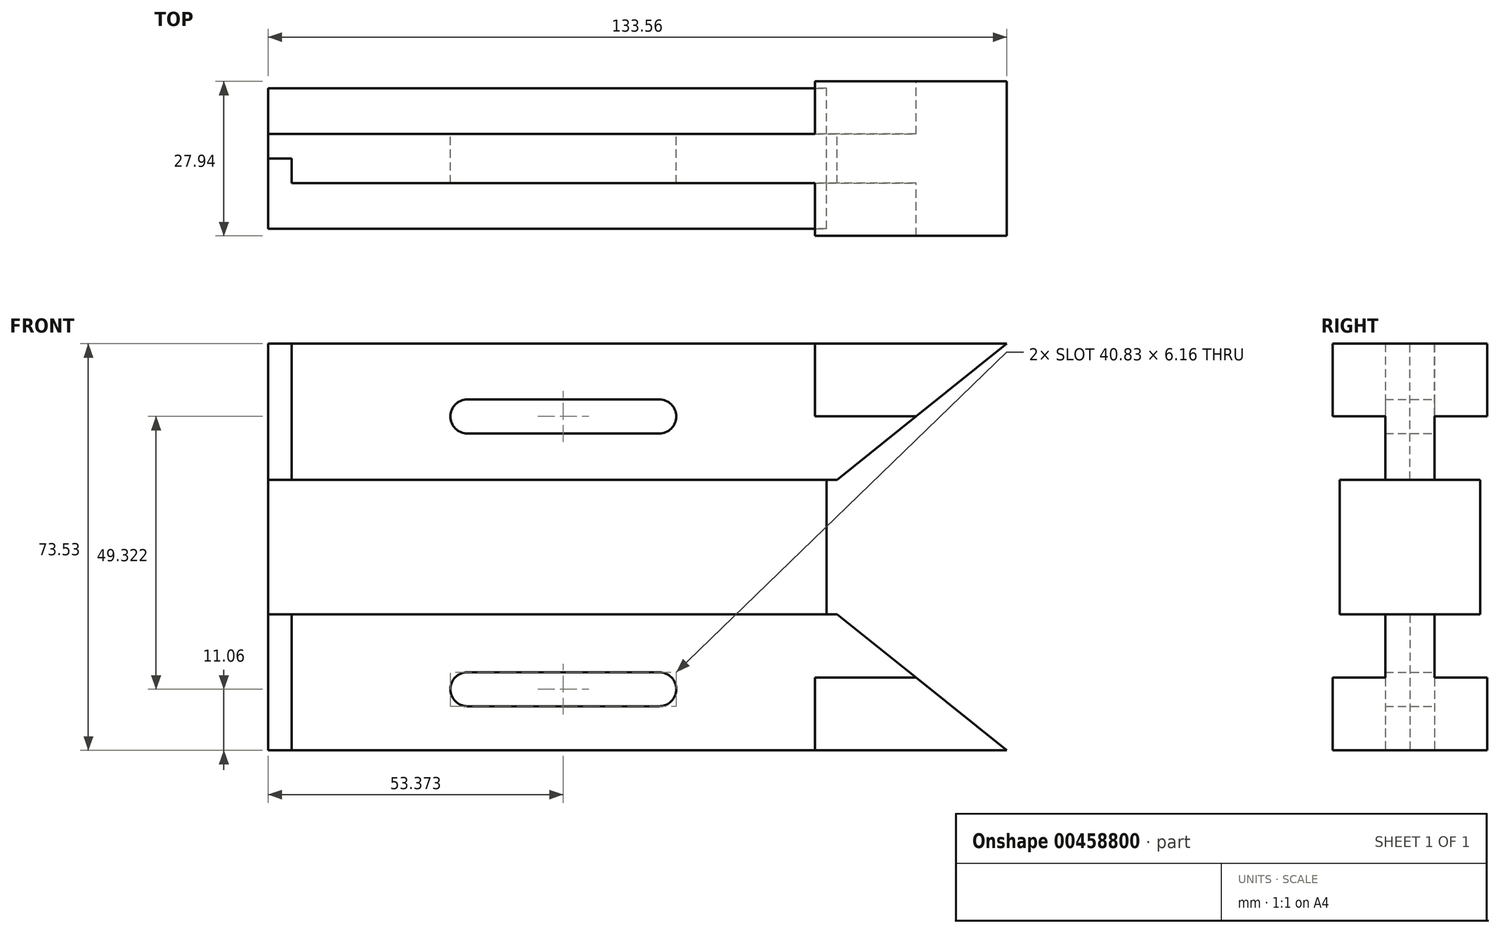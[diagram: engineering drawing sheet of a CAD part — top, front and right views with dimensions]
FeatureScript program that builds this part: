
annotation { "Feature Type Name" : "Feature", "Feature Type Description" : "" }
export const myFeature = defineFeature(function(context is Context, id is Id, definition is map)
    precondition{}
    {
        {
            var Q0;
            Q0=qCreatedBy(makeId("Front.planeOp"),FACE);
            var sketch = newSketch(context, id + "F0", { "sketchPlane" : qUnion([Q0])});
            skLineSegment(sketch, "E0", {"start": v(-65.14, 62.47) * mm, "end": v(68.42, 62.47) * mm});
            skLineSegment(sketch, "E1", {"start": v(68.42, 62.47) * mm, "end": v(68.42, 37.88) * mm});
            skLineSegment(sketch, "E2", {"start": v(68.42, 37.88) * mm, "end": v(-65.14, 37.88) * mm});
            skLineSegment(sketch, "E3", {"start": v(-65.14, 37.88) * mm, "end": v(-65.14, 62.47) * mm});
            skLineSegment(sketch, "E4", {"start": v(-65.14, 37.88) * mm, "end": v(-65.14, 25.7) * mm});
            skLineSegment(sketch, "E5", {"start": v(-65.14, 25.7) * mm, "end": v(35.8, 25.7) * mm});
            skLineSegment(sketch, "E6", {"start": v(35.8, 25.7) * mm, "end": v(35.8, 37.88) * mm});
            skLineSegment(sketch, "E7", {"start": v(-60.87, 62.47) * mm, "end": v(-60.87, 37.88) * mm});
            skLineSegment(sketch, "E8", {"start": v(33.75, 62.47) * mm, "end": v(33.75, 49.32) * mm});
            skArc(sketch, "E9", {"start": v(5.57, 46.24) * mm, "mid": v(8.65, 49.32) * mm, "end": v(5.57, 52.4) * mm});
            skArc(sketch, "E10", {"start": v(-29.1, 52.4) * mm, "mid": v(-32.18, 49.32) * mm, "end": v(-29.1, 46.24) * mm});
            skLineSegment(sketch, "E11", {"start": v(-29.1, 52.4) * mm, "end": v(5.57, 52.4) * mm});
            skLineSegment(sketch, "E12", {"start": v(-29.1, 46.24) * mm, "end": v(5.57, 46.24) * mm});
            skLineSegment(sketch, "E13", {"start": v(68.42, 62.47) * mm, "end": v(37.74, 37.88) * mm});
            skLineSegment(sketch, "E14", {"start": v(33.75, 49.32) * mm, "end": v(52.01, 49.32) * mm});
            skLineSegment(sketch, "E15", {"start": v(-65.14, 25.7) * mm, "end": v(-65.14, 13.53) * mm});
            skLineSegment(sketch, "E16", {"start": v(-65.14, 13.53) * mm, "end": v(35.8, 13.53) * mm});
            skLineSegment(sketch, "E17", {"start": v(35.8, 13.53) * mm, "end": v(35.8, 25.7) * mm});
            skLineSegment(sketch, "E18", {"start": v(-65.14, 13.53) * mm, "end": v(-65.14, -11.06) * mm});
            skLineSegment(sketch, "E19", {"start": v(-65.14, -11.06) * mm, "end": v(68.42, -11.06) * mm});
            skLineSegment(sketch, "E20", {"start": v(68.42, -11.06) * mm, "end": v(68.42, 13.53) * mm});
            skLineSegment(sketch, "E21", {"start": v(68.42, 13.53) * mm, "end": v(35.8, 13.53) * mm});
            skLineSegment(sketch, "E22", {"start": v(-60.87, 13.53) * mm, "end": v(-60.87, -11.06) * mm});
            skLineSegment(sketch, "E23", {"start": v(68.42, -11.06) * mm, "end": v(37.74, 13.53) * mm});
            skLineSegment(sketch, "E24", {"start": v(52.01, 2.09) * mm, "end": v(33.75, 2.09) * mm});
            skLineSegment(sketch, "E25", {"start": v(33.75, 2.09) * mm, "end": v(33.75, -11.06) * mm});
            skArc(sketch, "E26", {"start": v(-29.1, 3.08) * mm, "mid": v(-32.18, 0) * mm, "end": v(-29.1, -3.08) * mm});
            skArc(sketch, "E27", {"start": v(5.57, -3.08) * mm, "mid": v(8.65, 0) * mm, "end": v(5.57, 3.08) * mm});
            skLineSegment(sketch, "E28", {"start": v(-29.1, 3.08) * mm, "end": v(5.57, 3.08) * mm});
            skLineSegment(sketch, "E29", {"start": v(-29.1, -3.08) * mm, "end": v(5.57, -3.08) * mm});
            skSolve(sketch);
        }
        {
            var Q0;
            {var subQ0=sQuery(id+"F0.wireOp",EDGE,"E4");Q0=makeQuery(id+"F0.imprint","IMPRINT",FACE,{"disambiguationData":[TD([[makeQuery(id+"F0.imprint","IMPRINT",EDGE,{"derivedFrom":subQ0}),1.0]])]});}
            var Q1;
            Q1=makeQuery(id+"F0.imprint","IMPRINT",FACE,{"disambiguationData":[TD([[makeQuery(id+"F0.imprint","IMPRINT",EDGE,{"derivedFrom":sQuery(id+"F0.wireOp",EDGE,"E5")}),-1.0]])]});
            extrude(context, id + "F1", {"entities" : qUnion([Q0, Q1]), "depth" : 25.4 * mm, "symmetric" : true});
        }
        {
            var Q0;
            {var subQ0=sQuery(id+"F0.wireOp",EDGE,"E3");Q0=makeQuery(id+"F0.imprint","IMPRINT",FACE,{"disambiguationData":[TD([[makeQuery(id+"F0.imprint","IMPRINT",EDGE,{"derivedFrom":subQ0}),-1.0]])]});}
            var Q1;
            {var subQ0=sQuery(id+"F0.wireOp",EDGE,"E18");Q1=makeQuery(id+"F0.imprint","IMPRINT",FACE,{"disambiguationData":[TD([[makeQuery(id+"F0.imprint","IMPRINT",EDGE,{"derivedFrom":subQ0}),1.0]])]});}
            extrude(context, id + "F2", {"entities" : qUnion([Q0, Q1]), "operationType" : NewBodyOperationType.ADD, "oppositeDirection" : true, "depth" : 4.44 * mm});
        }
        {
            var Q0;
            {var subQ6=sQuery(id+"F0.wireOp",EDGE,"E7");Q0=makeQuery(id+"F0.imprint","IMPRINT",FACE,{"disambiguationData":[TD([[makeQuery(id+"F0.imprint","IMPRINT",EDGE,{"derivedFrom":subQ6}),1.0]])]});}
            var Q1;
            {var subQ7=sQuery(id+"F0.wireOp",EDGE,"E22");Q1=makeQuery(id+"F0.imprint","IMPRINT",FACE,{"disambiguationData":[TD([[makeQuery(id+"F0.imprint","IMPRINT",EDGE,{"derivedFrom":subQ7}),1.0]])]});}
            extrude(context, id + "F3", {"entities" : qUnion([Q0, Q1]), "operationType" : NewBodyOperationType.ADD, "depth" : 8.9 * mm, "symmetric" : true});
        }
        {
            var Q0;
            {var subQ3=sQuery(id+"F0.wireOp",EDGE,"E8");Q0=makeQuery(id+"F0.imprint","IMPRINT",FACE,{"disambiguationData":[TD([[makeQuery(id+"F0.imprint","IMPRINT",EDGE,{"derivedFrom":subQ3}),1.0]])]});}
            var Q1;
            {var subQ4=sQuery(id+"F0.wireOp",EDGE,"E24");Q1=makeQuery(id+"F0.imprint","IMPRINT",FACE,{"disambiguationData":[TD([[makeQuery(id+"F0.imprint","IMPRINT",EDGE,{"derivedFrom":subQ4}),1.0]])]});}
            extrude(context, id + "F4", {"entities" : qUnion([Q0, Q1]), "operationType" : NewBodyOperationType.ADD, "depth" : 27.94 * mm, "symmetric" : true});
        }
    });
